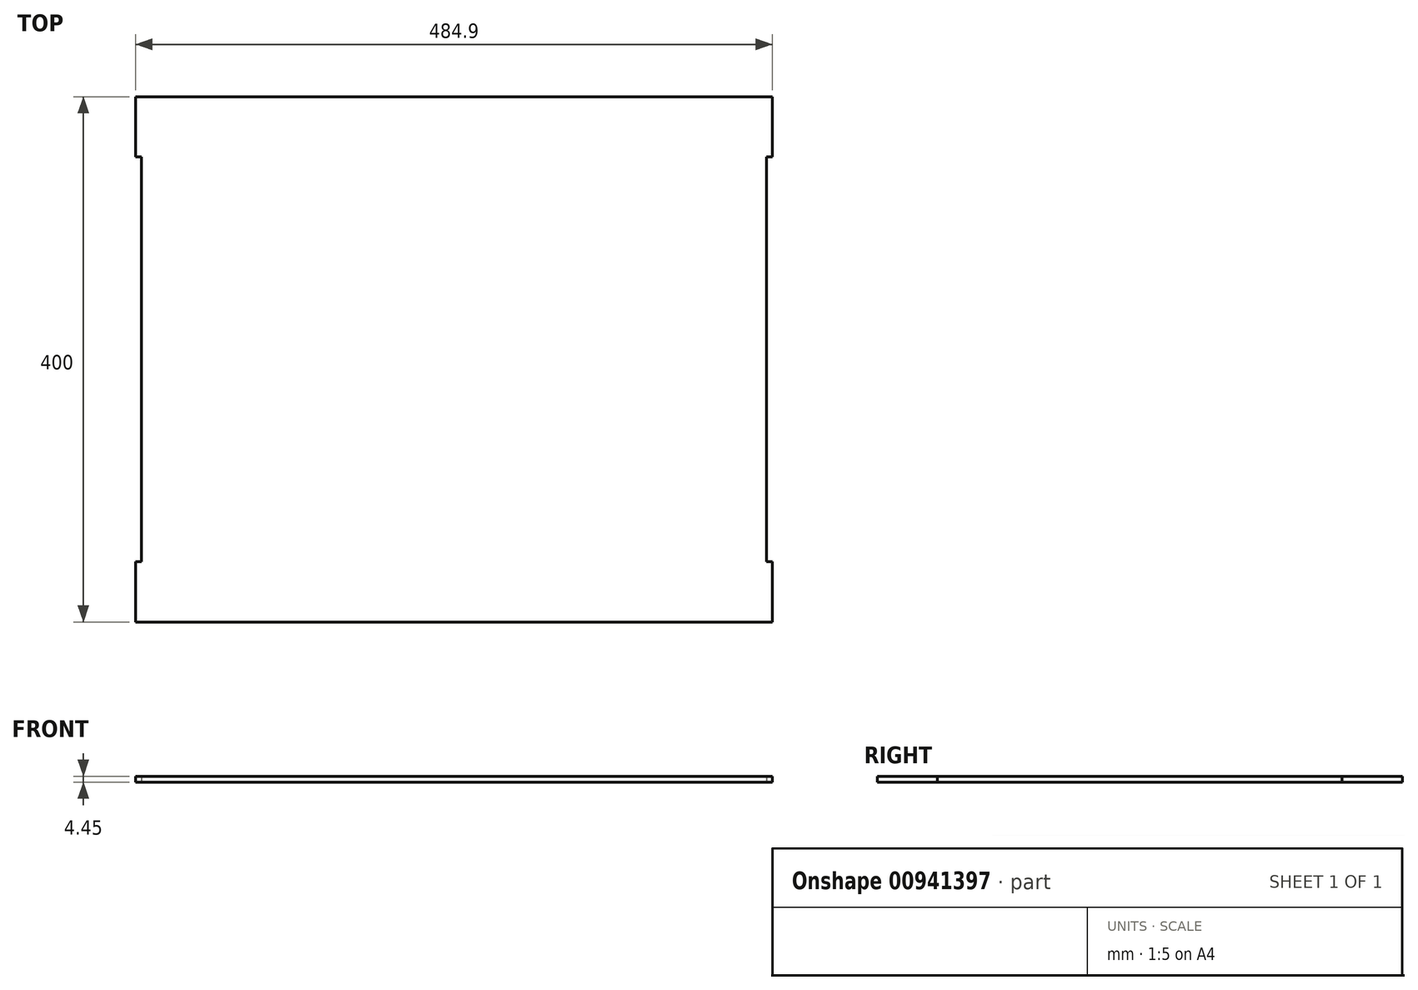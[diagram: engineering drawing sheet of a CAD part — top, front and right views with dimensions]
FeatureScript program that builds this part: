
annotation { "Feature Type Name" : "Feature", "Feature Type Description" : "" }
export const myFeature = defineFeature(function(context is Context, id is Id, definition is map)
    precondition{}
    {
        {
            var Q0;
            Q0=qCreatedBy(makeId("Top.planeOp"),FACE);
            var sketch = newSketch(context, id + "F0", { "sketchPlane" : qUnion([Q0])});
            skLineSegment(sketch, "E0.left", {"start": v(50.27, -200) * mm, "end": v(50.27, -154.1) * mm});
            skLineSegment(sketch, "E1.bottom", {"start": v(54.72, -154.1) * mm, "end": v(50.27, -154.1) * mm});
            skLineSegment(sketch, "E1.top", {"start": v(54.72, 154.1) * mm, "end": v(50.27, 154.1) * mm});
            skPoint(sketch, "E1.middle", {"position": v(50.27, 0) * mm});
            skPoint(sketch, "E1.right.end.orphan", {"position": v(45.82, 154.1) * mm});
            skPoint(sketch, "E2.orphan", {"position": v(45.82, -154.1) * mm});
            skLineSegment(sketch, "E3.trimOffspring", {"start": v(50.27, 154.1) * mm, "end": v(50.27, 200) * mm});
            skLineSegment(sketch, "E4.bottom", {"start": v(50.27, 200) * mm, "end": v(54.72, 200) * mm});
            skLineSegment(sketch, "E4.top", {"start": v(50.27, 154.1) * mm, "end": v(54.72, 154.1) * mm});
            skLineSegment(sketch, "E4.left", {"start": v(50.27, 200) * mm, "end": v(50.27, 154.1) * mm});
            skLineSegment(sketch, "E5.bottom", {"start": v(50.27, -200) * mm, "end": v(54.72, -200) * mm});
            skLineSegment(sketch, "E5.top", {"start": v(50.27, -154.1) * mm, "end": v(54.72, -154.1) * mm});
            skLineSegment(sketch, "E6.bottom", {"start": v(54.72, 200) * mm, "end": v(530.72, 200) * mm});
            skLineSegment(sketch, "E6.left", {"start": v(54.72, 154.1) * mm, "end": v(54.72, -154.1) * mm});
            skLineSegment(sketch, "E6.right", {"start": v(530.72, 154.1) * mm, "end": v(530.72, -154.1) * mm});
            skLineSegment(sketch, "E7.bottom", {"start": v(530.72, 154.1) * mm, "end": v(535.17, 154.1) * mm});
            skLineSegment(sketch, "E7.top", {"start": v(530.72, 200) * mm, "end": v(535.17, 200) * mm});
            skLineSegment(sketch, "E7.right", {"start": v(535.17, 154.1) * mm, "end": v(535.17, 200) * mm});
            skLineSegment(sketch, "E8.MirrorCS", {"start": v(530.72, -154.1) * mm, "end": v(535.17, -154.1) * mm});
            skLineSegment(sketch, "E9.MirrorCS", {"start": v(535.17, -154.1) * mm, "end": v(535.17, -200) * mm});
            skLineSegment(sketch, "E10.MirrorCS", {"start": v(530.72, -200) * mm, "end": v(535.17, -200) * mm});
            skPoint(sketch, "E6.top.end.orphan", {"position": v(530.72, -200) * mm});
            skLineSegment(sketch, "E11", {"start": v(54.72, -200) * mm, "end": v(530.72, -200) * mm});
            skSolve(sketch);
        }
        {
            var Q0;
            Q0=makeQuery(id+"F0.imprint","IMPRINT",FACE,{"disambiguationData":[TD([[makeQuery(id+"F0.imprint","IMPRINT",EDGE,{"derivedFrom":sQuery(id+"F0.wireOp",EDGE,"E4.bottom")}),-1.0]])]});
            extrude(context, id + "F1", {"entities" : qUnion([Q0]), "depth" : 4.45 * mm, "offsetDistance" : 25 * mm});
        }
    });
